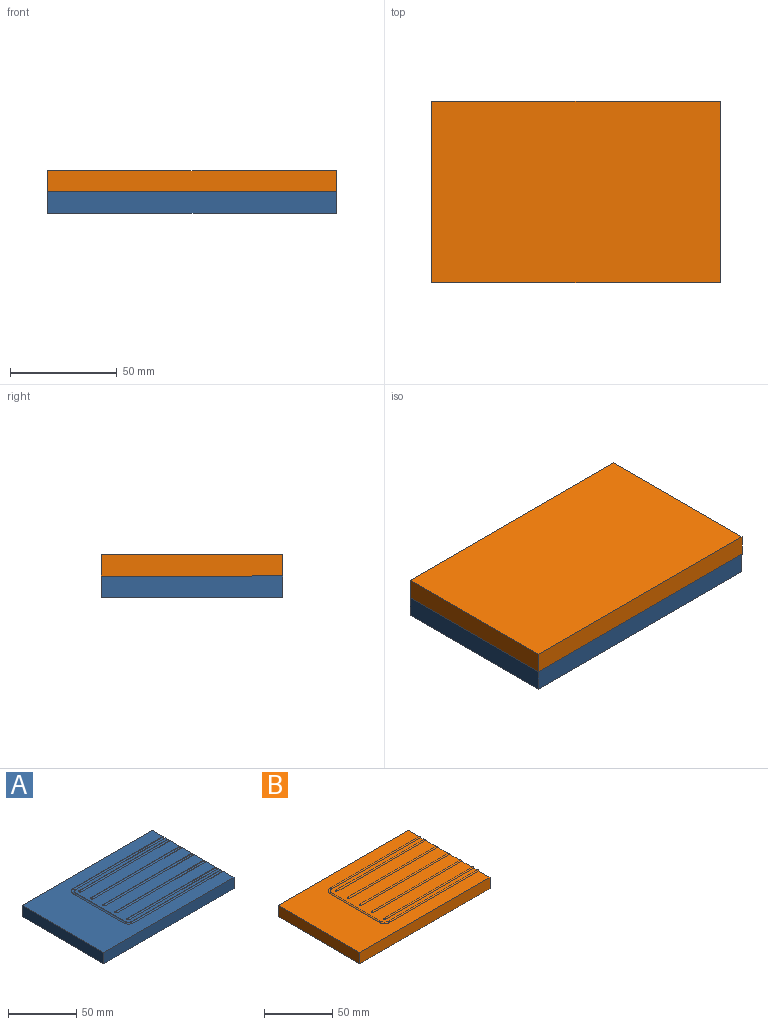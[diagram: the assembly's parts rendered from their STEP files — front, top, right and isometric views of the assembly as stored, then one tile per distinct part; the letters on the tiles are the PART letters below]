
ASSEMBLY  parts=2 mates=1
PART A: 47 faces, bbox 135x85x10 mm
  f0: plane 95.82x57.63mm, normal (0,0,1), area 4419.3mm2, adj f1,f22,f23,f24,f25,f26,f32,f33
  f1: plane 85x10mm, normal (1,0,0), area 838.9mm2, adj f0,f2,f3,f5,f6,f7,f11,f12
  f2: plane 135x10mm, normal (0,-1,0), area 1350mm2, adj f1,f4,f5,f6
  f3: plane 135x10mm, normal (0,1,0), area 1350mm2, adj f1,f4,f5,f6
  f4: plane 85x10mm, normal (-1,0,0), area 850mm2, adj f2,f3,f5,f6
  f5: plane 135x85mm, normal (0,0,-1), area 11475mm2, adj f1,f2,f3,f4
  f6: plane 135x85mm, normal (0,0,1), area 5363.2mm2, adj f1,f2,f3,f4,f27,f28,f29,f30
  f7: cylinder r=1mm len=93mm, axis (-1,0,0), area 261mm2, adj f1,f8,f22,f27
  f8: torus R=4mm, axis (0,0,-1), area 17.6mm2, adj f7,f9,f23,f28
  f9: cylinder r=1mm len=52mm, axis (0,1,0), area 145.9mm2, adj f8,f10,f24,f29
  f10: torus R=4mm, axis (0,0,-1), area 17.6mm2, adj f9,f11,f25,f30
  f11: cylinder r=1mm len=93mm, axis (1,0,0), area 261mm2, adj f1,f10,f26,f31
  f12: cylinder r=1mm len=92mm, axis (-1,0,0), area 258.2mm2, adj f1,f21,f44,f46
  f13: cylinder r=1mm len=92mm, axis (-1,0,0), area 258.2mm2, adj f1,f20,f41,f43
  f14: cylinder r=1mm len=92mm, axis (-1,0,0), area 258.2mm2, adj f1,f19,f38,f40
  f15: cylinder r=1mm len=92mm, axis (-1,0,0), area 258.2mm2, adj f1,f18,f35,f37
  f16: cylinder r=1mm len=92mm, axis (-1,0,0), area 258.2mm2, adj f1,f17,f32,f34
  f17: sphere r=1mm, area 2.6mm2, adj f16,f33
  f18: sphere r=1mm, area 2.6mm2, adj f15,f36
  f19: sphere r=1mm, area 2.6mm2, adj f14,f39
  f20: sphere r=1mm, area 2.6mm2, adj f13,f42
  f21: sphere r=1mm, area 2.6mm2, adj f12,f45
  f22: cylinder r=0.2mm len=93mm, axis (-1,0,0), area 26.1mm2, adj f0,f1,f7,f23
  f23: torus R=2.82mm, axis (0,0,-1), area 1.3mm2, adj f0,f8,f22,f24
  f24: cylinder r=0.2mm len=52mm, axis (0,1,0), area 14.6mm2, adj f0,f9,f23,f25
  f25: torus R=2.82mm, axis (0,0,-1), area 1.3mm2, adj f0,f10,f24,f26
  f26: cylinder r=0.2mm len=93mm, axis (1,0,0), area 26.1mm2, adj f0,f1,f11,f25
  f27: cylinder r=0.2mm len=93mm, axis (-1,0,0), area 26.1mm2, adj f1,f6,f7,f28
  f28: torus R=5.18mm, axis (0,0,1), area 2.2mm2, adj f6,f8,f27,f29
  f29: cylinder r=0.2mm len=52mm, axis (0,1,0), area 14.6mm2, adj f6,f9,f28,f30
  f30: torus R=5.18mm, axis (0,0,1), area 2.2mm2, adj f6,f10,f29,f31
  f31: cylinder r=0.2mm len=93mm, axis (1,0,0), area 26.1mm2, adj f1,f6,f11,f30
  f32: cylinder r=0.2mm len=92mm, axis (-1,0,0), area 25.8mm2, adj f0,f1,f16,f33
  f33: torus R=1.18mm, axis (0,0,1), area 0.9mm2, adj f0,f17,f32,f34
  f34: cylinder r=0.2mm len=92mm, axis (-1,0,0), area 25.8mm2, adj f0,f1,f16,f33
  f35: cylinder r=0.2mm len=92mm, axis (-1,0,0), area 25.8mm2, adj f0,f1,f15,f36
  f36: torus R=1.18mm, axis (0,0,1), area 0.9mm2, adj f0,f18,f35,f37
  f37: cylinder r=0.2mm len=92mm, axis (-1,0,0), area 25.8mm2, adj f0,f1,f15,f36
  f38: cylinder r=0.2mm len=92mm, axis (-1,0,0), area 25.8mm2, adj f0,f1,f14,f39
  f39: torus R=1.18mm, axis (0,0,1), area 0.9mm2, adj f0,f19,f38,f40
  f40: cylinder r=0.2mm len=92mm, axis (-1,0,0), area 25.8mm2, adj f0,f1,f14,f39
  f41: cylinder r=0.2mm len=92mm, axis (-1,0,0), area 25.8mm2, adj f0,f1,f13,f42
  f42: torus R=1.18mm, axis (0,0,1), area 0.9mm2, adj f0,f20,f41,f43
  f43: cylinder r=0.2mm len=92mm, axis (-1,0,0), area 25.8mm2, adj f0,f1,f13,f42
  f44: cylinder r=0.2mm len=92mm, axis (-1,0,0), area 25.8mm2, adj f0,f1,f12,f45
  f45: torus R=1.18mm, axis (0,0,1), area 0.9mm2, adj f0,f21,f44,f46
  f46: cylinder r=0.2mm len=92mm, axis (-1,0,0), area 25.8mm2, adj f0,f1,f12,f45
PART B: 22 faces, bbox 135x85x10.7 mm
  f0: plane 96.3x58.6mm, normal (0,0,1), area 4989.8mm2, adj f2,f7,f8,f9,f10,f11,f12,f13
  f1: plane 135x10mm, normal (0,-1,0), area 1350mm2, adj f2,f4,f5,f6
  f2: plane 85x10.7mm, normal (1,0,0), area 855.4mm2, adj f0,f1,f3,f5,f6,f7,f11,f12
  f3: plane 135x10mm, normal (0,1,0), area 1350mm2, adj f2,f4,f5,f6
  f4: plane 85x10mm, normal (-1,0,0), area 850mm2, adj f1,f3,f5,f6
  f5: plane 135x85mm, normal (0,0,-1), area 11475mm2, adj f1,f2,f3,f4
  f6: plane 135x85mm, normal (0,0,1), area 5487mm2, adj f1,f2,f3,f4,f7,f8,f9,f10
  f7: cylinder r=0.7mm len=92.7mm, axis (-1,0,0), area 203.9mm2, adj f0,f2,f6,f8
  f8: torus R=4.3mm, axis (0,0,-1), area 14.9mm2, adj f0,f6,f7,f9
  f9: cylinder r=0.7mm len=51.4mm, axis (0,1,0), area 113mm2, adj f0,f6,f8,f10
  f10: torus R=4.3mm, axis (0,0,-1), area 14.9mm2, adj f0,f6,f9,f11
  f11: cylinder r=0.7mm len=92.7mm, axis (1,0,0), area 203.9mm2, adj f0,f2,f6,f10
  f12: cylinder r=0.7mm len=92mm, axis (-1,0,0), area 202.3mm2, adj f0,f2,f21
  f13: cylinder r=0.7mm len=92mm, axis (-1,0,0), area 202.3mm2, adj f0,f2,f20
  f14: cylinder r=0.7mm len=92mm, axis (-1,0,0), area 202.3mm2, adj f0,f2,f19
  f15: cylinder r=0.7mm len=92mm, axis (-1,0,0), area 202.3mm2, adj f0,f2,f18
  f16: cylinder r=0.7mm len=92mm, axis (-1,0,0), area 202.3mm2, adj f0,f2,f17
  f17: sphere r=0.7mm, area 1.5mm2, adj f0,f16
  f18: sphere r=0.7mm, area 1.5mm2, adj f0,f15
  f19: sphere r=0.7mm, area 1.5mm2, adj f0,f14
  f20: sphere r=0.7mm, area 1.5mm2, adj f0,f13
  f21: sphere r=0.7mm, area 1.5mm2, adj f0,f12
PLACE A t=(34.06,94.31,42.45)mm fixed
PLACE B rot(axis=(1,0,0),180deg) t=(34.06,94.31,42.45)mm
MATE slider A.f39 <-> B.f0  axis (0,0,1) through (-6.94,94.31,42.45)mm
